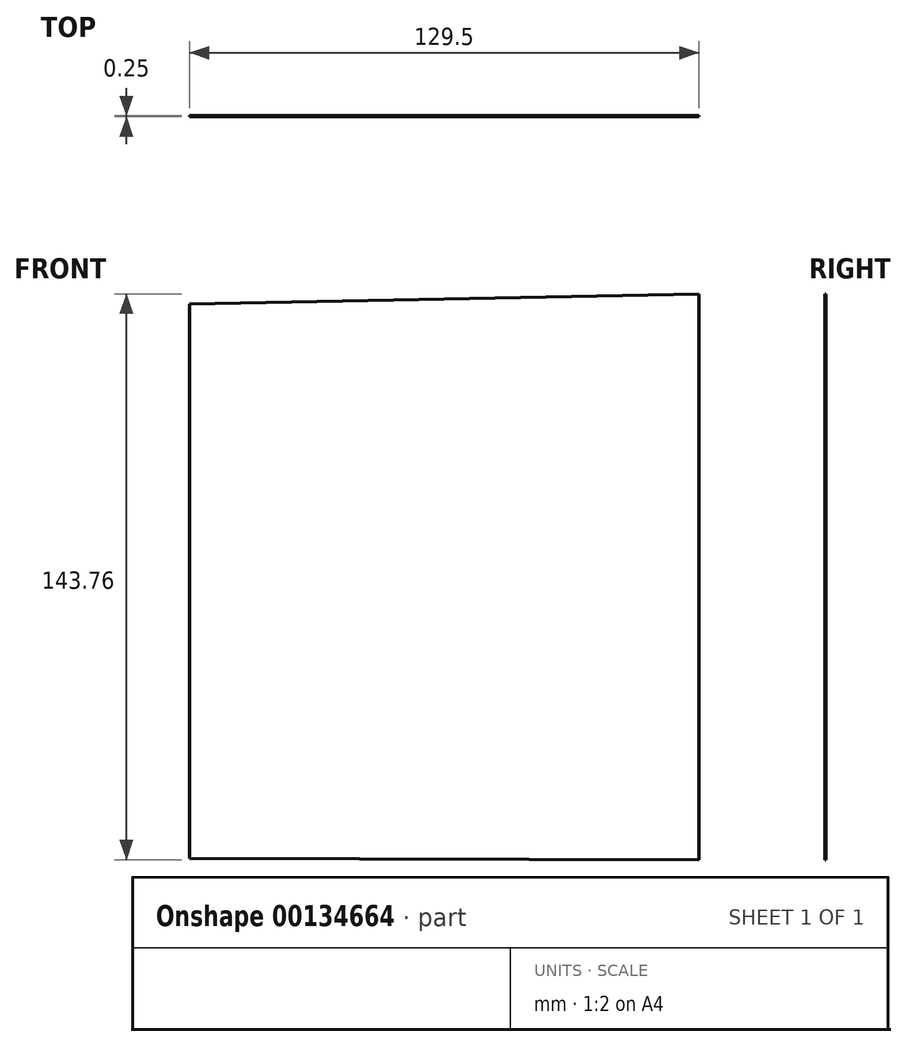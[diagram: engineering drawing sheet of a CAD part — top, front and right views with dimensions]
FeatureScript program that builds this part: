
annotation { "Feature Type Name" : "Feature", "Feature Type Description" : "" }
export const myFeature = defineFeature(function(context is Context, id is Id, definition is map)
    precondition{}
    {
        {
            var Q0;
            Q0=qCreatedBy(makeId("Front.planeOp"),FACE);
            var sketch = newSketch(context, id + "F0", { "sketchPlane" : qUnion([Q0])});
            skLineSegment(sketch, "E0", {"start": v(-56.05, -73.88) * mm, "end": v(-56.05, 67.03) * mm});
            skLineSegment(sketch, "E1", {"start": v(-56.05, 67.03) * mm, "end": v(73.45, 69.6) * mm});
            skLineSegment(sketch, "E2", {"start": v(73.45, 69.6) * mm, "end": v(73.45, -74.16) * mm});
            skLineSegment(sketch, "E3", {"start": v(-56.05, -73.88) * mm, "end": v(73.45, -74.16) * mm});
            skLineSegment(sketch, "E4", {"start": v(-76.3, 0) * mm, "end": v(76.59, 0) * mm});
            skSolve(sketch);
        }
        {
            var Q0;
            {var subQ0=sQuery(id+"F0.wireOp",EDGE,"E1");Q0=makeQuery(id+"F0.imprint","IMPRINT",FACE,{"disambiguationData":[TD([[makeQuery(id+"F0.imprint","IMPRINT",EDGE,{"derivedFrom":subQ0}),-1.0]])]});}
            var Q1;
            {var subQ0=sQuery(id+"F0.wireOp",EDGE,"E3");Q1=makeQuery(id+"F0.imprint","IMPRINT",FACE,{"disambiguationData":[TD([[makeQuery(id+"F0.imprint","IMPRINT",EDGE,{"derivedFrom":subQ0}),1.0]])]});}
            extrude(context, id + "F1", {"entities" : qUnion([Q0, Q1]), "depth" : 0.25 * mm});
        }
    });
